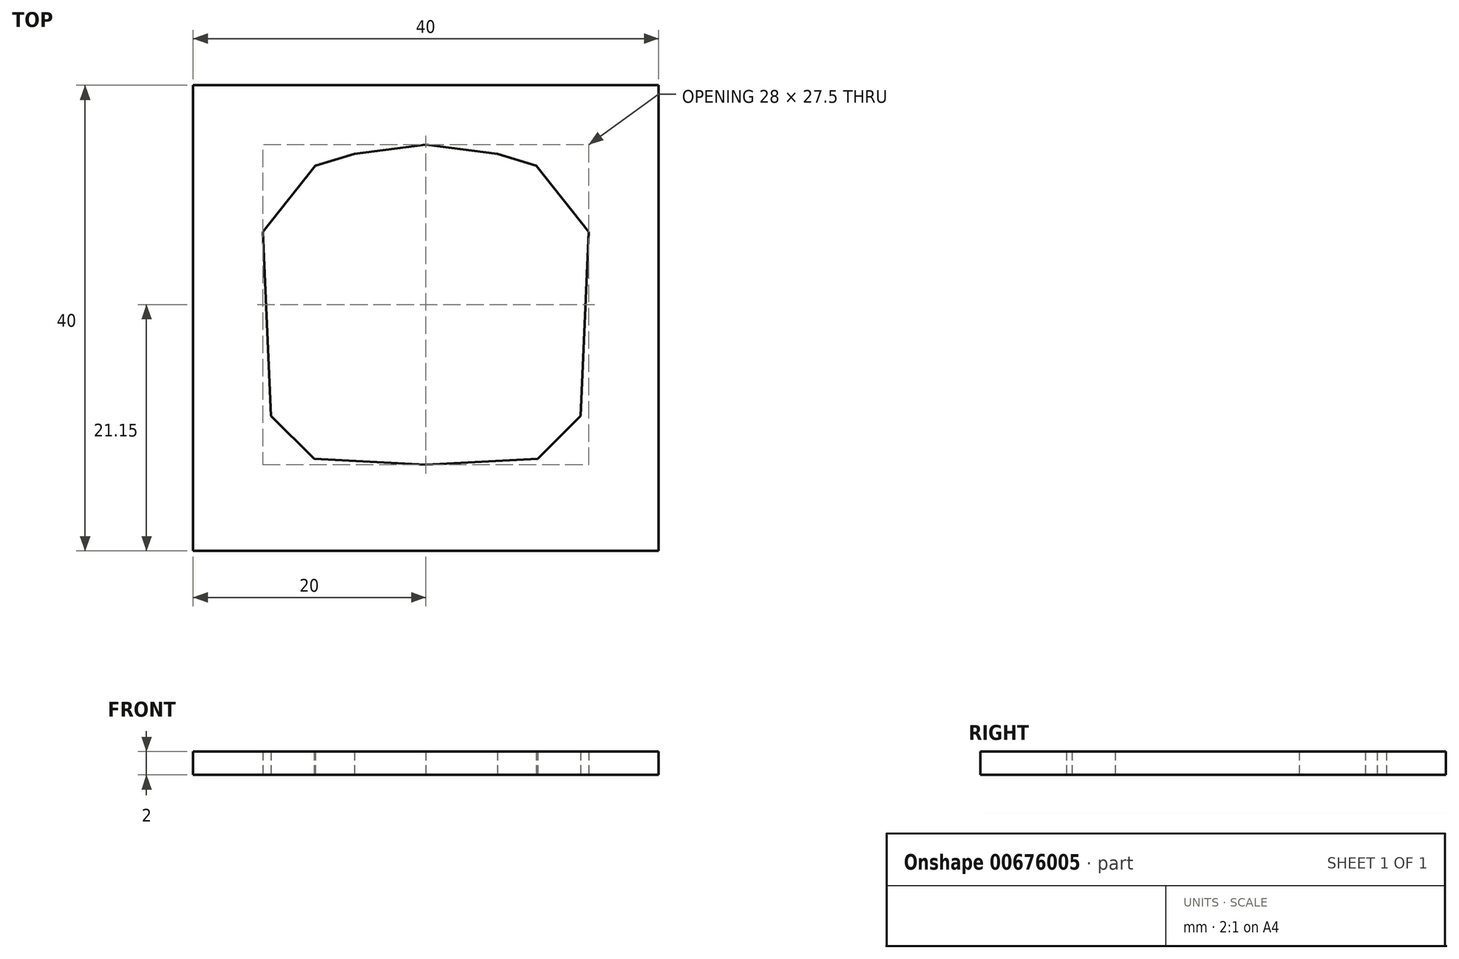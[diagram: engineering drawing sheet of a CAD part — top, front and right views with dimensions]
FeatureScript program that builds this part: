
annotation { "Feature Type Name" : "Feature", "Feature Type Description" : "" }
export const myFeature = defineFeature(function(context is Context, id is Id, definition is map)
    precondition{}
    {
        {
            var Q0;
            Q0=qCreatedBy(makeId("Top.planeOp"),FACE);
            var sketch = newSketch(context, id + "F0", { "sketchPlane" : qUnion([Q0])});
            skLineSegment(sketch, "E0", {"start": v(9.6, -4.98) * mm, "end": v(9.6, 5.13) * mm, "construction": true});
            skLineSegment(sketch, "E1", {"start": v(8.35, 0.5) * mm, "end": v(23.28, 0.5) * mm, "construction": true});
            skPoint(sketch, "E2", {"position": v(9.6, 0.5) * mm});
            skLineSegment(sketch, "E3", {"start": v(5.3, 4.2) * mm, "end": v(29, 4.2) * mm, "construction": true});
            skLineSegment(sketch, "E4", {"start": v(13.3, 12.3) * mm, "end": v(13.3, -14.93) * mm, "construction": true});
            skPoint(sketch, "E5", {"position": v(13.3, 4.2) * mm});
            skPoint(sketch, "E6", {"position": v(0, 27.5) * mm});
            skLineSegment(sketch, "E7", {"start": v(14, 34.55) * mm, "end": v(14, 19.23) * mm, "construction": true});
            skLineSegment(sketch, "E8", {"start": v(5.18, 20) * mm, "end": v(31.31, 20) * mm, "construction": true});
            skPoint(sketch, "E9", {"position": v(14, 20) * mm});
            skPoint(sketch, "E10", {"position": v(9.5, 25.7) * mm});
            skLineSegment(sketch, "E11", {"start": v(9.5, 25.7) * mm, "end": v(14, 20) * mm});
            skLineSegment(sketch, "E12", {"start": v(14, 20) * mm, "end": v(13.3, 4.2) * mm});
            skLineSegment(sketch, "E13", {"start": v(13.3, 4.2) * mm, "end": v(9.6, 0.5) * mm});
            skLineSegment(sketch, "E14", {"start": v(9.6, 0.5) * mm, "end": v(0, 0) * mm});
            skLineSegment(sketch, "E15", {"start": v(0, -7.4) * mm, "end": v(20, -7.4) * mm});
            skLineSegment(sketch, "E16", {"start": v(20, -7.4) * mm, "end": v(20, 32.6) * mm});
            skLineSegment(sketch, "E17", {"start": v(20, 32.6) * mm, "end": v(0, 32.6) * mm});
            skLineSegment(sketch, "E18.MirrorCS", {"start": v(-20, -7.4) * mm, "end": v(-20, 32.6) * mm});
            skLineSegment(sketch, "E19.MirrorCS", {"start": v(-20, 32.6) * mm, "end": v(0, 32.6) * mm});
            skLineSegment(sketch, "E20.MirrorCS", {"start": v(0, -7.4) * mm, "end": v(-20, -7.4) * mm});
            skLineSegment(sketch, "E21.MirrorCS", {"start": v(-9.6, 0.5) * mm, "end": v(0, 0) * mm});
            skLineSegment(sketch, "E22.MirrorCS", {"start": v(-13.3, 4.2) * mm, "end": v(-9.6, 0.5) * mm});
            skLineSegment(sketch, "E23.MirrorCS", {"start": v(-14, 20) * mm, "end": v(-13.3, 4.2) * mm});
            skLineSegment(sketch, "E24.MirrorCS", {"start": v(-9.5, 25.7) * mm, "end": v(-14, 20) * mm});
            skPoint(sketch, "E25", {"position": v(6.15, 26.7) * mm});
            skLineSegment(sketch, "E26", {"start": v(0, 27.5) * mm, "end": v(6.15, 26.7) * mm});
            skLineSegment(sketch, "E27", {"start": v(6.15, 26.7) * mm, "end": v(9.5, 25.7) * mm});
            skLineSegment(sketch, "E28.MirrorCS", {"start": v(0, 27.5) * mm, "end": v(-6.15, 26.7) * mm});
            skLineSegment(sketch, "E29.MirrorCS", {"start": v(-6.15, 26.7) * mm, "end": v(-9.5, 25.7) * mm});
            skSolve(sketch);
        }
        {
            var Q0;
            Q0=makeQuery(id+"F0.imprint","IMPRINT",FACE,{"disambiguationData":[TD([[makeQuery(id+"F0.imprint","IMPRINT",EDGE,{"derivedFrom":sQuery(id+"F0.wireOp",EDGE,"E11")}),1.0]])]});
            extrude(context, id + "F1", {"entities" : qUnion([Q0]), "depth" : 2 * mm, "offsetDistance" : 25 * mm});
        }
    });
